# Revit family: RobeHook_SurfaceMount_Abey_Vela
name_source: partatom
category: Specialty Equipment
units: mm (PartAtom-declared; Revit-internal decimal feet)

## family parameters
Always vertical = Yes
Cut with Voids When Loaded = No
OmniClass Number = 23.31.25.00
OmniClass Title = Toilet and Bath Specialties
Part Type = Normal
Room Calculation Point = No
Round Connector Dimension = Use Diameter
Shared = No
Work Plane-Based = No

## types (5) — shared parameters
Assembly Code = C1030210
IfcExportAs = IfcFurniture
IfcExportType = NOTDEFINED
Manufacturer = Abey
ManufacturerOverallDepth = 36 mm  [stored 0.11811 ft]
ManufacturerOverallHeight = 54 mm  [stored 0.177165 ft]
ManufacturerOverallWidth = 25 mm  [stored 0.082021 ft]
ManufacturerURLProductSpecific = https://www.abey.com.au
ModifiedIssue = 20241025 $
URL = https://www.abey.com.au
Uniclass2015Code = Pr_40_30_78_15
Uniclass2015Title = Clothes hooks
Uniclass2015Version = Products v1.33
zero-valued in all types: Default Elevation

## per-type parameters (varying)
| type | Description | ManufacturerSpecCode | Material | Model | Type Comments |
| Black (VRH-B) | Vela Robe Hook Black | VRH-B | Metal_Abey_Black | VRH-B | Black |
| Brushed Brass (VRH-BB) | Vela Robe Hook Brushed Brass | VRH-BB | Metal_Abey_Brass | VRH-BB | Brushed Brass |
| Gun Metal (VRH-GM) | Vela Robe Hook Gun Metal | VRH-GM | Metal_Abey_GunMetal | VRH-GM | Gun Metal |
| Brushed Nickel (VRH-BN) | Vela Robe Hook Brushed Nickel | VRH-BN | Metal_Abey_BrushedNickel | VRH-BN | Brushed Nickel |
| Chrome (VRH) | Vela Robe Hook Chrome | VRH | Metal_Abey_Chrome | VRH | Chrome |

note: [stored X ft] marks values corroborated as IEEE doubles in the binary element streams (Revit-internal decimal feet)

## geometry (parser evidence)
native form markers: Sweep x2
no freeform markers — native parametric forms only
